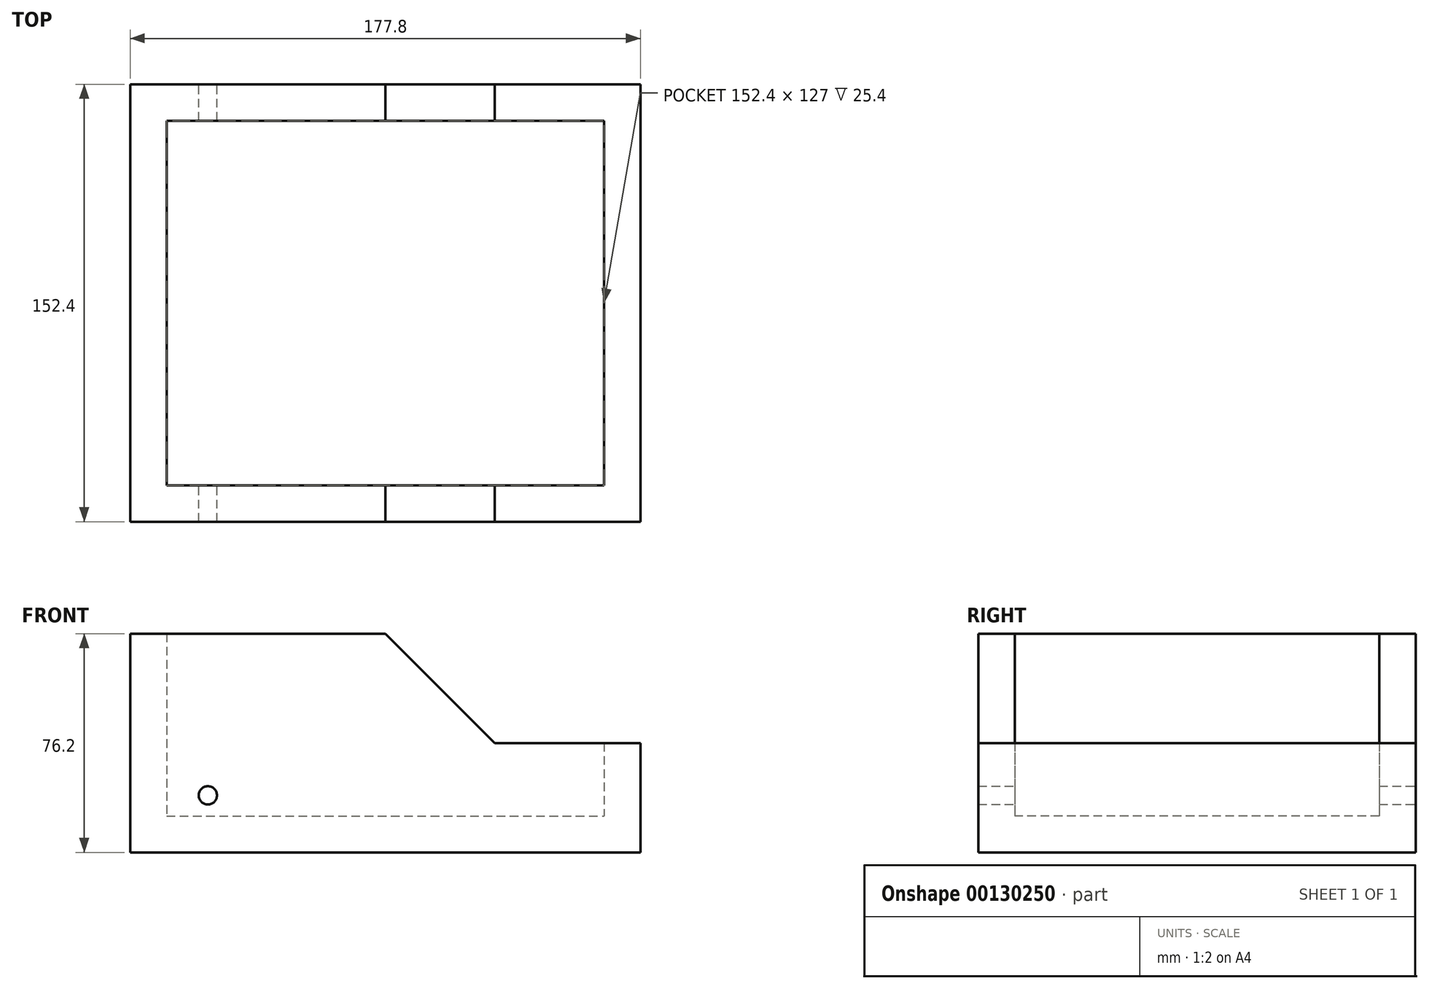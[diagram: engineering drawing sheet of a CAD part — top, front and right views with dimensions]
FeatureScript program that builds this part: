
annotation { "Feature Type Name" : "Feature", "Feature Type Description" : "" }
export const myFeature = defineFeature(function(context is Context, id is Id, definition is map)
    precondition{}
    {
        {
            var Q0;
            Q0=qCreatedBy(makeId("Top.planeOp"),FACE);
            var sketch = newSketch(context, id + "F0", { "sketchPlane" : qUnion([Q0])});
            skLineSegment(sketch, "E0.bottom", {"start": v(88.9, -76.2) * mm, "end": v(-88.9, -76.2) * mm});
            skLineSegment(sketch, "E0.top", {"start": v(88.9, 76.2) * mm, "end": v(-88.9, 76.2) * mm});
            skLineSegment(sketch, "E0.left", {"start": v(88.9, -76.2) * mm, "end": v(88.9, 76.2) * mm});
            skLineSegment(sketch, "E0.right", {"start": v(-88.9, -76.2) * mm, "end": v(-88.9, 76.2) * mm});
            skPoint(sketch, "E0.middle", {"position": v(0, 0) * mm});
            skLineSegment(sketch, "E1", {"start": v(38.1, 76.2) * mm, "end": v(38.1, -76.2) * mm});
            skLineSegment(sketch, "E2.bottom", {"start": v(-76.2, 63.5) * mm, "end": v(76.2, 63.5) * mm});
            skLineSegment(sketch, "E2.top", {"start": v(-76.2, -63.5) * mm, "end": v(76.2, -63.5) * mm});
            skLineSegment(sketch, "E2.left", {"start": v(-76.2, 63.5) * mm, "end": v(-76.2, -63.5) * mm});
            skLineSegment(sketch, "E2.right", {"start": v(76.2, 63.5) * mm, "end": v(76.2, -63.5) * mm});
            skSolve(sketch);
        }
        {
            var Q0;
            {var subQ0=sQuery(id+"F0.wireOp",EDGE,"E0.right");Q0=makeQuery(id+"F0.imprint","IMPRINT",FACE,{"disambiguationData":[TD([[makeQuery(id+"F0.imprint","IMPRINT",EDGE,{"derivedFrom":subQ0}),-1.0]])]});}
            extrude(context, id + "F1", {"entities" : qUnion([Q0]), "depth" : 76.2 * mm});
        }
        {
            var Q0;
            {var subQ0=sQuery(id+"F0.wireOp",EDGE,"E0.left");Q0=makeQuery(id+"F0.imprint","IMPRINT",FACE,{"disambiguationData":[TD([[makeQuery(id+"F0.imprint","IMPRINT",EDGE,{"derivedFrom":subQ0}),1.0]])]});}
            extrude(context, id + "F2", {"entities" : qUnion([Q0]), "depth" : 38.1 * mm});
        }
        {
            var Q0;
            Q0=makeQuery(id+"F1.opExtrude","CAP_EDGE",EDGE,{"disambiguationData":[OSD([sQuery(id+"F0.wireOp",EDGE,"E1")])],"isStart":false});
            chamfer(context, id + "F3", {"entities" : qUnion([Q0]), "width" : 38.1 * mm, "tangentPropagation" : true});
        }
        {
            var Q0;
            Q0=makeQuery(id+"F0.imprint","IMPRINT",FACE,{"disambiguationData":[TD([[makeQuery(id+"F0.imprint","IMPRINT",EDGE,{"derivedFrom":sQuery(id+"F0.wireOp",EDGE,"E2.bottom")}),-1.0]])]});
            extrude(context, id + "F4", {"entities" : qUnion([Q0]), "operationType" : NewBodyOperationType.ADD, "depth" : 12.7 * mm});
        }
        {
            var Q0;
            Q0=makeQuery(id+"F1.opExtrude","SWEPT_FACE",FACE,{"disambiguationData":[OSD([sQuery(id+"F0.wireOp",EDGE,"E0.top")])]});
            var sketch = newSketch(context, id + "F5", { "sketchPlane" : qUnion([Q0])});
            skCircle(sketch, "E3", {"center": v(61.81, 19.86) * mm, "radius": 3.18 * mm});
            skSolve(sketch);
        }
        {
            var Q0;
            Q0=sQuery(id+"F5.wireOp",VERTEX,"E3.center");
            var Q1;
            Q1=makeQuery(id+"F1.opExtrude","SWEPT_BODY",BODY,{"disambiguationData":[OSD([sQuery(id+"F0.wireOp",EDGE,"E0.bottom"),sQuery(id+"F0.wireOp",EDGE,"E0.top"),sQuery(id+"F0.wireOp",EDGE,"E0.right"),sQuery(id+"F0.wireOp",EDGE,"E1"),sQuery(id+"F0.wireOp",EDGE,"E2.bottom"),sQuery(id+"F0.wireOp",EDGE,"E2.top"),sQuery(id+"F0.wireOp",EDGE,"E2.left"),sQuery(id+"F0.wireOp",EDGE,"E2.right")])]});
            hole(context, id + "F6", {"style" : HoleStyle.SIMPLE, "endStyle" : HoleEndStyle.THROUGH, "holeDiameter" : 6.35 * mm, "locations" : qUnion([Q0]), "scope" : qUnion([Q1]), "isTappedThrough" : true});
        }
    });
